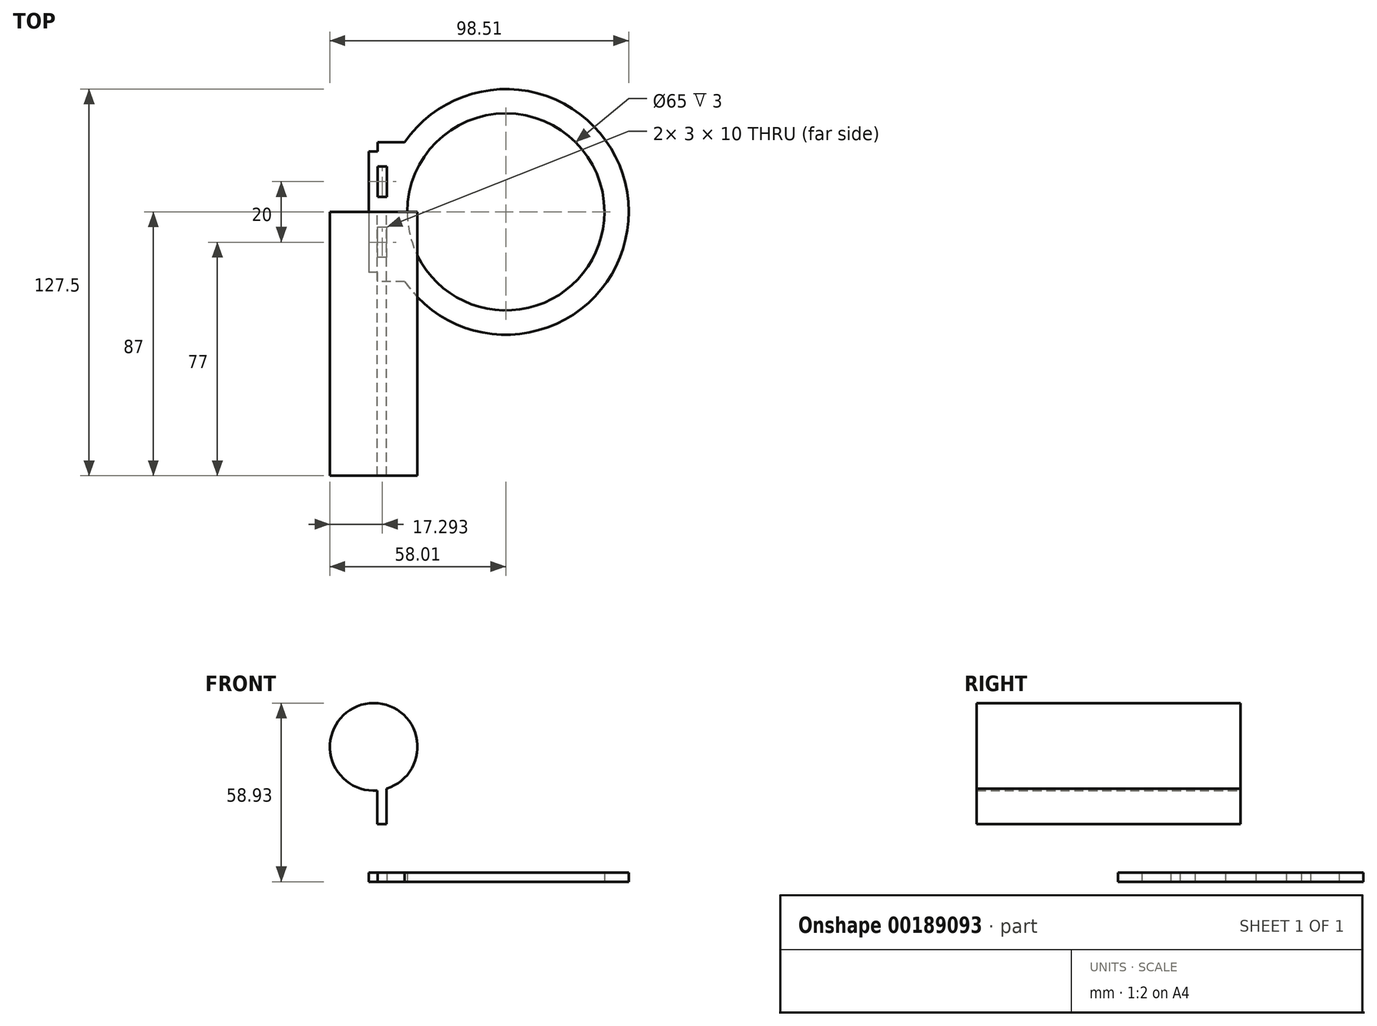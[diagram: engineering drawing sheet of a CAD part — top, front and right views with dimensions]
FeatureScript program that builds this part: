
annotation { "Feature Type Name" : "Feature", "Feature Type Description" : "" }
export const myFeature = defineFeature(function(context is Context, id is Id, definition is map)
    precondition{}
    {
        {
            var Q0;
            Q0=qCreatedBy(makeId("Top.planeOp"),FACE);
            var sketch = newSketch(context, id + "F0", { "sketchPlane" : qUnion([Q0])});
            skCircle(sketch, "E0", {"center": v(0, 0) * mm, "radius": 32.5 * mm});
            skArc(sketch, "E1.0", {"start": v(-33.34, -23) * mm, "mid": v(40.5, 0) * mm, "end": v(-33.34, 23) * mm});
            skLineSegment(sketch, "E2.bottom", {"start": v(-42.22, 20) * mm, "end": v(-45.22, 20) * mm});
            skLineSegment(sketch, "E2.top", {"start": v(-42.22, -20) * mm, "end": v(-45.22, -20) * mm});
            skLineSegment(sketch, "E2.right", {"start": v(-45.22, 20) * mm, "end": v(-45.22, -20) * mm});
            skLineSegment(sketch, "E3.bottom", {"start": v(-39.22, 15) * mm, "end": v(-42.22, 15) * mm});
            skLineSegment(sketch, "E3.left", {"start": v(-39.22, 15) * mm, "end": v(-39.22, 5) * mm});
            skLineSegment(sketch, "E3.right", {"start": v(-42.22, 15) * mm, "end": v(-42.22, 5) * mm});
            skLineSegment(sketch, "E4", {"start": v(-42.22, 5) * mm, "end": v(-39.22, 5) * mm});
            skLineSegment(sketch, "E5.MirrorCS", {"start": v(-39.22, -15) * mm, "end": v(-42.22, -15) * mm});
            skLineSegment(sketch, "E6.MirrorCS", {"start": v(-39.22, -15) * mm, "end": v(-39.22, -5) * mm});
            skLineSegment(sketch, "E7.MirrorCS", {"start": v(-42.22, -5) * mm, "end": v(-39.22, -5) * mm});
            skLineSegment(sketch, "E8.MirrorCS", {"start": v(-42.22, -15) * mm, "end": v(-42.22, -5) * mm});
            skLineSegment(sketch, "E9", {"start": v(-39.22, -23) * mm, "end": v(-33.34, -23) * mm});
            skLineSegment(sketch, "E10", {"start": v(-39.22, 23) * mm, "end": v(-33.34, 23) * mm});
            skPoint(sketch, "E11.orphan", {"position": v(-35.22, 20) * mm});
            skLineSegment(sketch, "E12", {"start": v(-39.22, -23) * mm, "end": v(-42.22, -23) * mm});
            skPoint(sketch, "E12.endSnap0", {"position": v(-42.22, -20) * mm});
            skLineSegment(sketch, "E13", {"start": v(-42.22, -23) * mm, "end": v(-42.22, -20) * mm});
            skLineSegment(sketch, "E14", {"start": v(-42.22, 20) * mm, "end": v(-42.22, 23) * mm});
            skLineSegment(sketch, "E15", {"start": v(-42.22, 23) * mm, "end": v(-39.22, 23) * mm});
            skSolve(sketch);
        }
        {
            var Q0;
            Q0=makeQuery(id+"F0.imprint","IMPRINT",FACE,{"disambiguationData":[TD([[makeQuery(id+"F0.imprint","IMPRINT",EDGE,{"derivedFrom":sQuery(id+"F0.wireOp",EDGE,"E0")}),-1.0]])]});
            extrude(context, id + "F1", {"entities" : qUnion([Q0]), "depth" : 3 * mm});
        }
        {
            var Q0;
            Q0=qCreatedBy(makeId("Front.planeOp"),FACE);
            var sketch = newSketch(context, id + "F2", { "sketchPlane" : qUnion([Q0])});
            skArc(sketch, "E16", {"start": v(-39.35, 30.68) * mm, "mid": v(-46.31, 58.66) * mm, "end": v(-42.35, 30.1) * mm});
            skLineSegment(sketch, "E17.bottom", {"start": v(-42.35, 18.94) * mm, "end": v(-39.35, 18.94) * mm});
            skLineSegment(sketch, "E17.left", {"start": v(-42.35, 18.94) * mm, "end": v(-42.35, 30.1) * mm});
            skLineSegment(sketch, "E17.right", {"start": v(-39.35, 18.94) * mm, "end": v(-39.35, 30.68) * mm});
            skSolve(sketch);
        }
        {
            var Q0;
            Q0=makeQuery(id+"F2.imprint","IMPRINT",FACE,{"disambiguationData":[TD([[makeQuery(id+"F2.imprint","IMPRINT",EDGE,{"derivedFrom":sQuery(id+"F2.wireOp",EDGE,"E16")}),1.0]])]});
            extrude(context, id + "F3", {"entities" : qUnion([Q0]), "depth" : 87 * mm});
        }
    });
